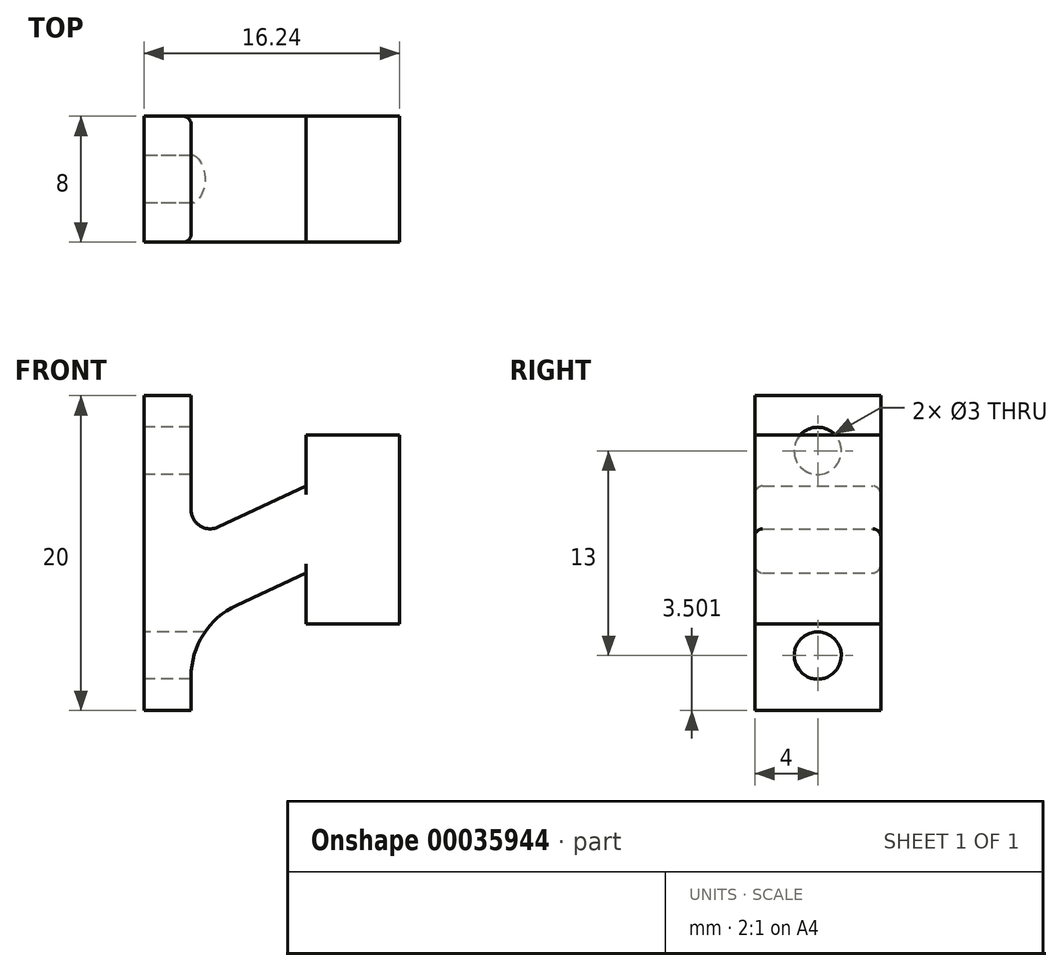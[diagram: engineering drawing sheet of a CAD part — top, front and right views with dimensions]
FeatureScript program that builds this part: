
annotation { "Feature Type Name" : "Feature", "Feature Type Description" : "" }
export const myFeature = defineFeature(function(context is Context, id is Id, definition is map)
    precondition{}
    {
        {
            var Q0;
            Q0=qCreatedBy(makeId("Front.planeOp"),FACE);
            var sketch = newSketch(context, id + "F0", { "sketchPlane" : qUnion([Q0])});
            skLineSegment(sketch, "E0", {"start": v(0, 14.47) * mm, "end": v(0, -5.53) * mm});
            skLineSegment(sketch, "E1", {"start": v(0, -5.53) * mm, "end": v(3, -5.53) * mm});
            skLineSegment(sketch, "E2", {"start": v(3, -5.53) * mm, "end": v(3, -3.38) * mm});
            skLineSegment(sketch, "E3", {"start": v(5.89, 1.15) * mm, "end": v(10.32, 3.22) * mm});
            skLineSegment(sketch, "E4", {"start": v(10.32, 3.22) * mm, "end": v(10.32, -0.02) * mm});
            skLineSegment(sketch, "E5", {"start": v(10.32, -0.02) * mm, "end": v(16.24, -0.02) * mm});
            skLineSegment(sketch, "E6", {"start": v(16.24, -0.02) * mm, "end": v(16.24, 11.98) * mm});
            skLineSegment(sketch, "E7", {"start": v(16.24, 11.98) * mm, "end": v(10.32, 11.98) * mm});
            skLineSegment(sketch, "E8", {"start": v(10.32, 11.98) * mm, "end": v(10.32, 8.74) * mm});
            skLineSegment(sketch, "E9", {"start": v(10.32, 8.74) * mm, "end": v(4.72, 6.13) * mm});
            skLineSegment(sketch, "E10", {"start": v(3, 7.23) * mm, "end": v(3, 14.47) * mm});
            skLineSegment(sketch, "E11", {"start": v(3, 14.47) * mm, "end": v(0, 14.47) * mm});
            skPoint(sketch, "E12.visualSharp", {"position": v(3, -0.2) * mm});
            skArc(sketch, "E12.filletArc", {"start": v(5.89, 1.15) * mm, "mid": v(3.78, -0.7) * mm, "end": v(3, -3.38) * mm});
            skPoint(sketch, "E13.visualSharp", {"position": v(3, 5.32) * mm});
            skArc(sketch, "E13.filletArc", {"start": v(3, 7.23) * mm, "mid": v(3.56, 6.2) * mm, "end": v(4.72, 6.13) * mm});
            skSolve(sketch);
        }
        {
            var Q0;
            Q0=makeQuery(id+"F0.imprint","IMPRINT",FACE,{"disambiguationData":[TD([[makeQuery(id+"F0.imprint","IMPRINT",EDGE,{"derivedFrom":sQuery(id+"F0.wireOp",EDGE,"E0")}),1.0]])]});
            extrude(context, id + "F1", {"entities" : qUnion([Q0]), "depth" : 8 * mm});
        }
        {
            var Q0;
            Q0=qCreatedBy(makeId("Right.planeOp"),FACE);
            var sketch = newSketch(context, id + "F2", { "sketchPlane" : qUnion([Q0])});
            skCircle(sketch, "E14", {"center": v(-4, -2.03) * mm, "radius": 1.5 * mm});
            skCircle(sketch, "E15", {"center": v(-4, 10.97) * mm, "radius": 1.5 * mm});
            skLineSegment(sketch, "E16", {"start": v(-4, 10.97) * mm, "end": v(-4, -2.03) * mm, "construction": true});
            skLineSegment(sketch, "E17", {"start": v(-4, 4.47) * mm, "end": v(-8, 4.47) * mm, "construction": true});
            skSolve(sketch);
        }
        {
            var Q0;
            Q0 = qSketchRegion(id + "F2", true);
            extrude(context, id + "F3", {"entities" : qUnion([Q0]), "operationType" : NewBodyOperationType.REMOVE, "endBound" : BoundingType.UP_TO_NEXT, "depth" : 25 * mm});
        }
        {
            var Q0;
            Q0=makeQuery(id+"F1.opExtrude","CAP_EDGE",EDGE,{"disambiguationData":[OSD([sQuery(id+"F0.wireOp",EDGE,"E9")])],"isStart":true});
            var Q1;
            Q1=makeQuery(id+"F1.opExtrude","CAP_EDGE",EDGE,{"disambiguationData":[OSD([sQuery(id+"F0.wireOp",EDGE,"E3")])],"isStart":true});
            var Q2;
            Q2=makeQuery(id+"F1.opExtrude","CAP_EDGE",EDGE,{"disambiguationData":[OSD([sQuery(id+"F0.wireOp",EDGE,"E9")])],"isStart":false});
            var Q3;
            Q3=makeQuery(id+"F1.opExtrude","CAP_EDGE",EDGE,{"disambiguationData":[OSD([sQuery(id+"F0.wireOp",EDGE,"E3")])],"isStart":false});
            fillet(context, id + "F4", {"entities" : qUnion([Q0, Q1, Q2, Q3]), "radius" : .5 * mm, "tangentPropagation" : true, "allowEdgeOverflow" : false});
        }
    });
